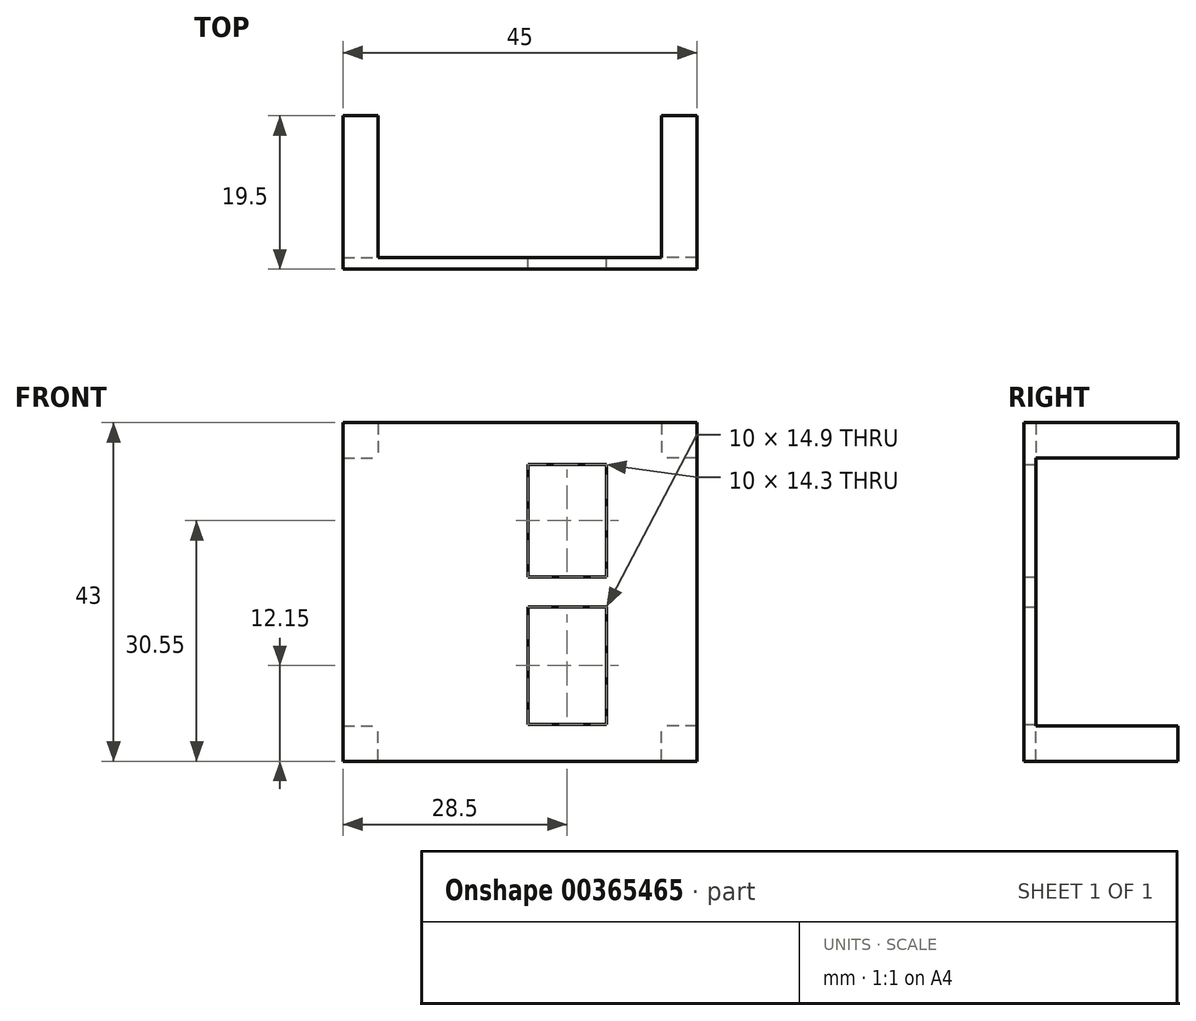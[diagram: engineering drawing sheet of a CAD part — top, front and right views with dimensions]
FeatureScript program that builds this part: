
annotation { "Feature Type Name" : "Feature", "Feature Type Description" : "" }
export const myFeature = defineFeature(function(context is Context, id is Id, definition is map)
    precondition{}
    {
        {
            var Q0;
            Q0=qCreatedBy(makeId("Front.planeOp"),FACE);
            var sketch = newSketch(context, id + "F0", { "sketchPlane" : qUnion([Q0])});
            skLineSegment(sketch, "E0.bottom", {"start": v(0, 0) * mm, "end": v(45, 0) * mm});
            skLineSegment(sketch, "E0.top", {"start": v(0, 43) * mm, "end": v(45, 43) * mm});
            skLineSegment(sketch, "E0.left", {"start": v(0, 0) * mm, "end": v(0, 43) * mm});
            skLineSegment(sketch, "E0.right", {"start": v(45, 0) * mm, "end": v(45, 43) * mm});
            skLineSegment(sketch, "E1", {"start": v(45, 43) * mm, "end": v(33.5, 43) * mm});
            skLineSegment(sketch, "E2", {"start": v(33.5, 43) * mm, "end": v(23.5, 43) * mm});
            skLineSegment(sketch, "E3", {"start": v(23.5, 37.7) * mm, "end": v(23.5, 23.4) * mm});
            skPoint(sketch, "E3.endSnap0", {"position": v(0, 21.5) * mm});
            skLineSegment(sketch, "E4", {"start": v(23.5, 19.6) * mm, "end": v(23.5, 4.7) * mm});
            skLineSegment(sketch, "E5", {"start": v(23.5, 4.7) * mm, "end": v(33.5, 4.7) * mm});
            skLineSegment(sketch, "E6", {"start": v(33.5, 4.7) * mm, "end": v(33.5, 19.6) * mm});
            skLineSegment(sketch, "E7", {"start": v(33.5, 37.7) * mm, "end": v(23.5, 37.7) * mm});
            skLineSegment(sketch, "E8.bottom", {"start": v(33.5, 19.6) * mm, "end": v(23.5, 19.6) * mm});
            skLineSegment(sketch, "E8.top", {"start": v(33.5, 23.4) * mm, "end": v(23.5, 23.4) * mm});
            skPoint(sketch, "E8.middle", {"position": v(23.5, 21.5) * mm});
            skPoint(sketch, "E8.right.end.orphan", {"position": v(13.5, 23.4) * mm});
            skPoint(sketch, "E8.right.start.orphan", {"position": v(13.5, 19.6) * mm});
            skLineSegment(sketch, "E9.trimOffspring", {"start": v(33.5, 23.4) * mm, "end": v(33.5, 37.7) * mm});
            skSolve(sketch);
        }
        {
            var Q0;
            Q0 = qSketchRegion(id + "F0", true);
            extrude(context, id + "F1", {"entities" : qUnion([Q0]), "depth" : 1.5 * mm});
        }
        {
            var Q0;
            Q0=makeQuery(id+"F1.opExtrude","CAP_FACE",FACE,{"disambiguationData":[OSD([sQuery(id+"F0.wireOp",EDGE,"E0.bottom"),sQuery(id+"F0.wireOp",EDGE,"E0.top"),sQuery(id+"F0.wireOp",EDGE,"E0.left"),sQuery(id+"F0.wireOp",EDGE,"E0.right")])],"isStart":true});
            var sketch = newSketch(context, id + "F2", { "sketchPlane" : qUnion([Q0])});
            skLineSegment(sketch, "E10.bottom", {"start": v(0, 43) * mm, "end": v(-4.5, 43) * mm});
            skLineSegment(sketch, "E10.top", {"start": v(0, 38.5) * mm, "end": v(-4.5, 38.5) * mm});
            skLineSegment(sketch, "E10.left", {"start": v(0, 43) * mm, "end": v(0, 38.5) * mm});
            skLineSegment(sketch, "E10.right", {"start": v(-4.5, 43) * mm, "end": v(-4.5, 38.5) * mm});
            skLineSegment(sketch, "E11.bottom", {"start": v(0, 0) * mm, "end": v(-4.5, 0) * mm});
            skLineSegment(sketch, "E11.top", {"start": v(0, 4.5) * mm, "end": v(-4.5, 4.5) * mm});
            skLineSegment(sketch, "E11.left", {"start": v(0, 0) * mm, "end": v(0, 4.5) * mm});
            skLineSegment(sketch, "E11.right", {"start": v(-4.5, 0) * mm, "end": v(-4.5, 4.5) * mm});
            skLineSegment(sketch, "E12", {"start": v(-22.5, 43) * mm, "end": v(-22.5, 40.3) * mm});
            skPoint(sketch, "E12.endSnap0", {"position": v(-22.5, 43) * mm});
            skLineSegment(sketch, "E13.MirrorCS", {"start": v(-45, 0) * mm, "end": v(-45, 4.5) * mm});
            skLineSegment(sketch, "E14.MirrorCS", {"start": v(-45, 4.5) * mm, "end": v(-40.5, 4.5) * mm});
            skLineSegment(sketch, "E15.MirrorCS", {"start": v(-40.5, 0) * mm, "end": v(-40.5, 4.5) * mm});
            skLineSegment(sketch, "E16.MirrorCS", {"start": v(-45, 0) * mm, "end": v(-40.5, 0) * mm});
            skLineSegment(sketch, "E17.MirrorCS", {"start": v(-40.5, 43) * mm, "end": v(-40.5, 38.5) * mm});
            skLineSegment(sketch, "E18.MirrorCS", {"start": v(-45, 43) * mm, "end": v(-45, 38.5) * mm});
            skLineSegment(sketch, "E19.MirrorCS", {"start": v(-45, 38.5) * mm, "end": v(-40.5, 38.5) * mm});
            skLineSegment(sketch, "E20.MirrorCS", {"start": v(-45, 43) * mm, "end": v(-40.5, 43) * mm});
            skSolve(sketch);
        }
        {
            var Q0;
            Q0 = qSketchRegion(id + "F2", true);
            extrude(context, id + "F3", {"entities" : qUnion([Q0]), "operationType" : NewBodyOperationType.ADD, "depth" : 18 * mm});
        }
    });
